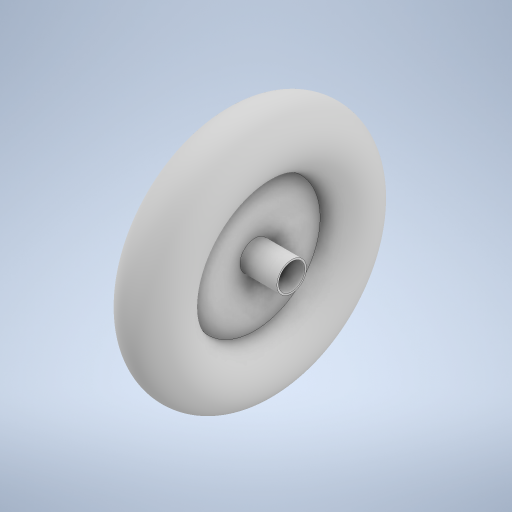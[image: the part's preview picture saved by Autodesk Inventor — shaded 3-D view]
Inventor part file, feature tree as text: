
AUTODESK INVENTOR PART (.ipt)
format: ipt  version: 2024 (Build 280153000, 153)  size: 319,488 bytes
history: native  units: in
note: dims shown in document units (in); Inventor stores cm internally (conversion verified against a paired STEP export)
features: sketch x5, extrude x4, revolve x1
ambient origin geometry x8: Origin, YZ Plane, XZ Plane, XY Plane, X Axis, Y Axis, Z Axis, Center Point
bodies: Body1 (feature_tree)
feature tree (10):
  sketch  "Sketch1"  dims[d1=3.0in d2=4.8in]
  revolve  "Revolution5"  [1 undecoded]
  extrude  "Extrusion1"  Depth=0.5in
  extrude  "Extrusion2"  Depth=1.5in
  extrude  "Extrusion3"  Depth=1.0in
  extrude  "Extrusion4"  Depth=1.5in
  sketch  "Sketch3"  dims[d4=0.5in d5=0.25in]
  sketch  "Sketch4"  dims[d9=90.0deg d10=1.5in]
  sketch  "Sketch5"  dims[d11=1.0in d12=0.0in d13=0.875in]
  sketch  "Sketch6"  dims[d14=1.0in d15=0.0in d16=1.5in d17=1.33in d18=1.875in d19=0.0in d20=3.0in d21=0.0in]
note: 1 required parameter value undecoded (feature->parameter linkage not recoverable at this tier; creation-order binding heuristic only, values carry confidence <= 0.55)
